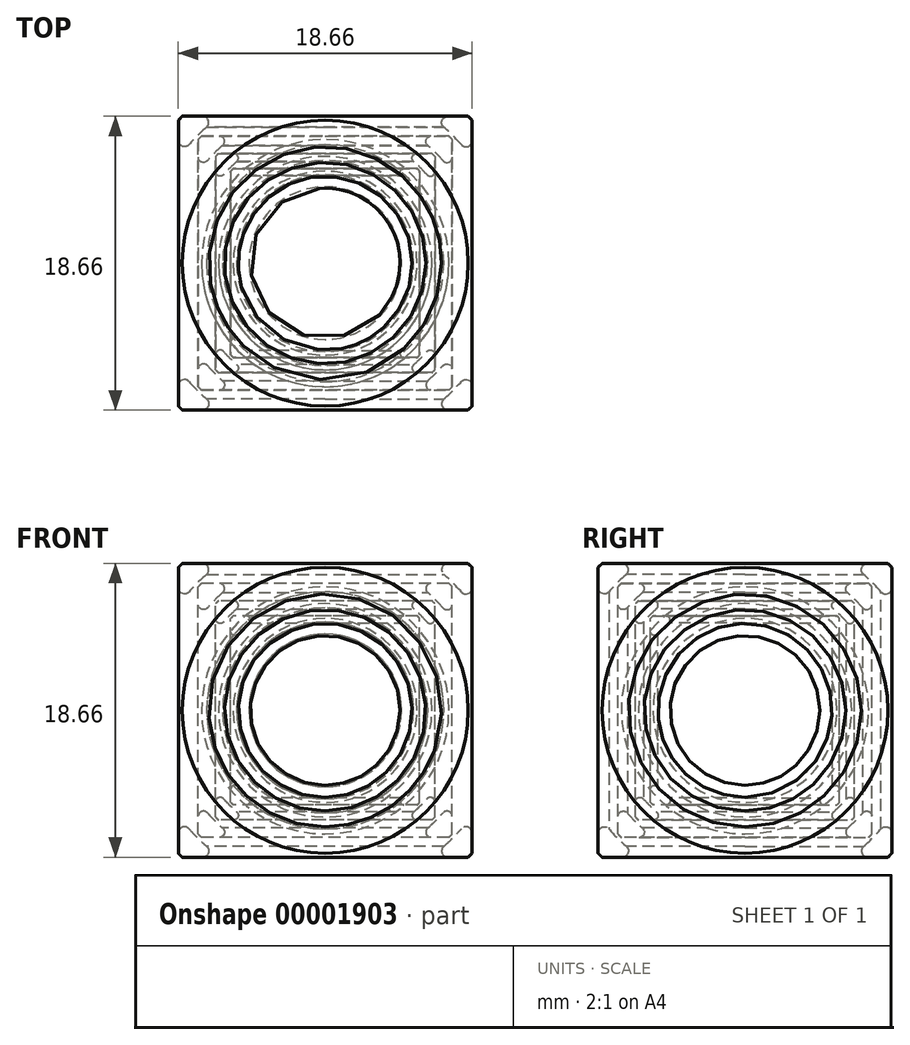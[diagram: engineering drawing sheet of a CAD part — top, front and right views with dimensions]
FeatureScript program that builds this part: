
annotation { "Feature Type Name" : "Feature", "Feature Type Description" : "" }
export const myFeature = defineFeature(function(context is Context, id is Id, definition is map)
    precondition{}
    {
        {
            var Q0;
            Q0=qCreatedBy(makeId("Top.planeOp"),FACE);
            var sketch = newSketch(context, id + "F0", { "sketchPlane" : qUnion([Q0])});
            skLineSegment(sketch, "E0.bottom", {"start": v(6, 6) * mm, "end": v(-6, 6) * mm});
            skLineSegment(sketch, "E0.top", {"start": v(6, -6) * mm, "end": v(-6, -6) * mm});
            skLineSegment(sketch, "E0.left", {"start": v(6, 6) * mm, "end": v(6, -6) * mm});
            skLineSegment(sketch, "E0.right", {"start": v(-6, 6) * mm, "end": v(-6, -6) * mm});
            skPoint(sketch, "E0.middle", {"position": v(0, 0) * mm});
            skCircle(sketch, "E1", {"center": v(0, 0) * mm, "radius": 7.38 * mm, "construction": true});
            skCircle(sketch, "E2", {"center": v(0, 0) * mm, "radius": 8.38 * mm, "construction": true});
            skLineSegment(sketch, "E3", {"start": v(-8.38, 0) * mm, "end": v(8.38, 0) * mm});
            skSolve(sketch);
        }
        {
            var Q0;
            {var subQ0=sQuery(id+"F0.wireOp",EDGE,"E0.bottom");Q0=makeQuery(id+"F0.imprint","IMPRINT",FACE,{"disambiguationData":[TD([[makeQuery(id+"F0.imprint","IMPRINT",EDGE,{"derivedFrom":subQ0}),1.0]])]});}
            var Q1;
            {var subQ0=sQuery(id+"F0.wireOp",EDGE,"E0.top");Q1=makeQuery(id+"F0.imprint","IMPRINT",FACE,{"disambiguationData":[TD([[makeQuery(id+"F0.imprint","IMPRINT",EDGE,{"derivedFrom":subQ0}),-1.0]])]});}
            extrude(context, id + "F1", {"entities" : qUnion([Q0, Q1]), "endBound" : BoundingType.SYMMETRIC, "depth" : 12 * mm});
        }
        {
            var Q0;
            Q0=qCreatedBy(makeId("Top.planeOp"),FACE);
            var sketch = newSketch(context, id + "F2", { "sketchPlane" : qUnion([Q0])});
            skCircle(sketch, "E4.0", {"center": v(0, 0) * mm, "radius": 8.38 * mm});
            skCircle(sketch, "E4.1", {"center": v(0, 0) * mm, "radius": 7.38 * mm});
            skLineSegment(sketch, "E4.2", {"start": v(-12.76, 0) * mm, "end": v(12.76, 0) * mm});
            skCircle(sketch, "E5", {"center": v(0, 0) * mm, "radius": 12.76 * mm});
            skPoint(sketch, "E6.orphan", {"position": v(-8.38, 0) * mm});
            skPoint(sketch, "E7.orphan", {"position": v(8.38, 0) * mm});
            skSolve(sketch);
        }
        {
            var Q0;
            {var subQ0=sQuery(id+"F2.wireOp",EDGE,"E4.2");var subQ1=sQuery(id+"F2.wireOp",EDGE,"E4.1");var subQ2=makeQuery(id+"F2.imprint","INTERSECT",VERTEX,{"disambiguationData":[OD(0.0)],"derivedFrom":[subQ1,subQ0]});Q0=makeQuery(id+"F2.imprint","IMPRINT",FACE,{"disambiguationData":[TD([[makeQuery(id+"F2.imprint","IMPRINT",EDGE,{"disambiguationData":[TD([[subQ2,1.0]])],"derivedFrom":subQ1}),1.0]])]});}
            var Q1;
            Q1=sQuery(id+"F2.wireOp",EDGE,"E4.2");
            revolve(context, id + "F3", {"operationType" : NewBodyOperationType.REMOVE, "entities" : qUnion([Q0]), "axis" : qUnion([Q1]), "revolveType" : RevolveType.FULL, "oppositeDirection" : true});
        }
        {
            var Q0;
            {var subQ0=sQuery(id+"F2.wireOp",EDGE,"E4.2");var subQ1=sQuery(id+"F2.wireOp",EDGE,"E4.0");var subQ2=makeQuery(id+"F2.imprint","INTERSECT",VERTEX,{"disambiguationData":[OD(0.0)],"derivedFrom":[subQ1,subQ0]});Q0=makeQuery(id+"F2.imprint","IMPRINT",FACE,{"disambiguationData":[TD([[makeQuery(id+"F2.imprint","IMPRINT",EDGE,{"disambiguationData":[TD([[subQ2,1.0]])],"derivedFrom":subQ1}),-1.0]])]});}
            var Q1;
            Q1=sQuery(id+"F2.wireOp",EDGE,"E4.2");
            revolve(context, id + "F4", {"operationType" : NewBodyOperationType.REMOVE, "entities" : qUnion([Q0]), "axis" : qUnion([Q1]), "revolveType" : RevolveType.FULL, "oppositeDirection" : true});
        }
        {
            var Q0;
            Q0=makeQuery(id+"F3.boolean.opBoolean","INTERSECT",EDGE,{"derivedFrom":[makeQuery(id+"F1.opExtrude","CAP_FACE",FACE,{"disambiguationData":[OSD([sQuery(id+"F0.wireOp",EDGE,"E0.bottom"),sQuery(id+"F0.wireOp",EDGE,"E0.top"),sQuery(id+"F0.wireOp",EDGE,"E0.left"),sQuery(id+"F0.wireOp",EDGE,"E0.right")])],"isStart":false}),makeQuery(id+"F3.opRevolve","SWEPT_FACE",FACE,{"disambiguationData":[OSD([sQuery(id+"F2.wireOp",EDGE,"E4.1")])]})]});
            var Q1;
            Q1=makeQuery(id+"F3.boolean.opBoolean","INTERSECT",EDGE,{"derivedFrom":[makeQuery(id+"F1.opExtrude","SWEPT_FACE",FACE,{"disambiguationData":[OSD([sQuery(id+"F0.wireOp",EDGE,"E0.bottom")])]}),makeQuery(id+"F3.opRevolve","SWEPT_FACE",FACE,{"disambiguationData":[OSD([sQuery(id+"F2.wireOp",EDGE,"E4.1")])]})]});
            var Q2;
            Q2=makeQuery(id+"F3.boolean.opBoolean","INTERSECT",EDGE,{"derivedFrom":[makeQuery(id+"F1.opExtrude","SWEPT_FACE",FACE,{"disambiguationData":[OSD([sQuery(id+"F0.wireOp",EDGE,"E0.top")])]}),makeQuery(id+"F3.opRevolve","SWEPT_FACE",FACE,{"disambiguationData":[OSD([sQuery(id+"F2.wireOp",EDGE,"E4.1")])]})]});
            var Q3;
            Q3=makeQuery(id+"F3.boolean.opBoolean","INTERSECT",EDGE,{"derivedFrom":[makeQuery(id+"F1.opExtrude","CAP_FACE",FACE,{"disambiguationData":[OSD([sQuery(id+"F0.wireOp",EDGE,"E0.bottom"),sQuery(id+"F0.wireOp",EDGE,"E0.top"),sQuery(id+"F0.wireOp",EDGE,"E0.left"),sQuery(id+"F0.wireOp",EDGE,"E0.right")])],"isStart":true}),makeQuery(id+"F3.opRevolve","SWEPT_FACE",FACE,{"disambiguationData":[OSD([sQuery(id+"F2.wireOp",EDGE,"E4.1")])]})]});
            var Q4;
            Q4=makeQuery(id+"F3.boolean.opBoolean","INTERSECT",EDGE,{"derivedFrom":[makeQuery(id+"F1.opExtrude","SWEPT_FACE",FACE,{"disambiguationData":[OSD([sQuery(id+"F0.wireOp",EDGE,"E0.right")])]}),makeQuery(id+"F3.opRevolve","SWEPT_FACE",FACE,{"disambiguationData":[OSD([sQuery(id+"F2.wireOp",EDGE,"E4.1")])]})]});
            var Q5;
            Q5=makeQuery(id+"F3.boolean.opBoolean","INTERSECT",EDGE,{"derivedFrom":[makeQuery(id+"F1.opExtrude","SWEPT_FACE",FACE,{"disambiguationData":[OSD([sQuery(id+"F0.wireOp",EDGE,"E0.left")])]}),makeQuery(id+"F3.opRevolve","SWEPT_FACE",FACE,{"disambiguationData":[OSD([sQuery(id+"F2.wireOp",EDGE,"E4.1")])]})]});
            fillet(context, id + "F5", {"entities" : qUnion([Q0, Q1, Q2, Q3, Q4, Q5]), "radius" : .25 * mm, "tangentPropagation" : true, "allowEdgeOverflow" : false});
        }
        {
            var Q0;
            Q0=makeQuery(id+"F1.opExtrude","SWEPT_BODY",BODY,{"disambiguationData":[OSD([sQuery(id+"F0.wireOp",EDGE,"E0.bottom"),sQuery(id+"F0.wireOp",EDGE,"E0.top"),sQuery(id+"F0.wireOp",EDGE,"E0.left"),sQuery(id+"F0.wireOp",EDGE,"E0.right")])]});
            var Q1;
            Q1=sQuery(id+"F0.wireOp",VERTEX,"E0.middle");
            transform(context, id + "F6", {"entities" : qUnion([Q0]), "transformType" : TransformType.SCALE_UNIFORMLY, "scale" : 1.16, "scalePoint" : qUnion([Q1]), "makeCopy" : true});
        }
        {
            var Q0;
            Q0=makeQuery(id+"F6.opPattern","COPY",BODY,{"derivedFrom":makeQuery(id+"F1.opExtrude","SWEPT_BODY",BODY,{"disambiguationData":[OSD([sQuery(id+"F0.wireOp",EDGE,"E0.bottom"),sQuery(id+"F0.wireOp",EDGE,"E0.top"),sQuery(id+"F0.wireOp",EDGE,"E0.left"),sQuery(id+"F0.wireOp",EDGE,"E0.right")])]}),"instanceName":"1"});
            var Q1;
            Q1=sQuery(id+"F0.wireOp",VERTEX,"E0.middle");
            transform(context, id + "F7", {"entities" : qUnion([Q0]), "transformType" : TransformType.SCALE_UNIFORMLY, "scale" : 1.16, "scalePoint" : qUnion([Q1]), "makeCopy" : true});
        }
        {
            var Q0;
            Q0=makeQuery(id+"F7.opPattern","COPY",BODY,{"derivedFrom":makeQuery(id+"F6.opPattern","COPY",BODY,{"derivedFrom":makeQuery(id+"F1.opExtrude","SWEPT_BODY",BODY,{"disambiguationData":[OSD([sQuery(id+"F0.wireOp",EDGE,"E0.bottom"),sQuery(id+"F0.wireOp",EDGE,"E0.top"),sQuery(id+"F0.wireOp",EDGE,"E0.left"),sQuery(id+"F0.wireOp",EDGE,"E0.right")])]}),"instanceName":"1"}),"instanceName":"1"});
            var Q1;
            Q1=sQuery(id+"F0.wireOp",VERTEX,"E0.middle");
            var Q2;
            Q2=sQuery(id+"F0.wireOp",VERTEX,"E0.middle");
            transform(context, id + "F8", {"entities" : qUnion([Q0]), "transformType" : TransformType.SCALE_UNIFORMLY, "scale" : 1.16, "scalePoint" : qUnion([Q2]), "makeCopy" : true});
        }
    });
